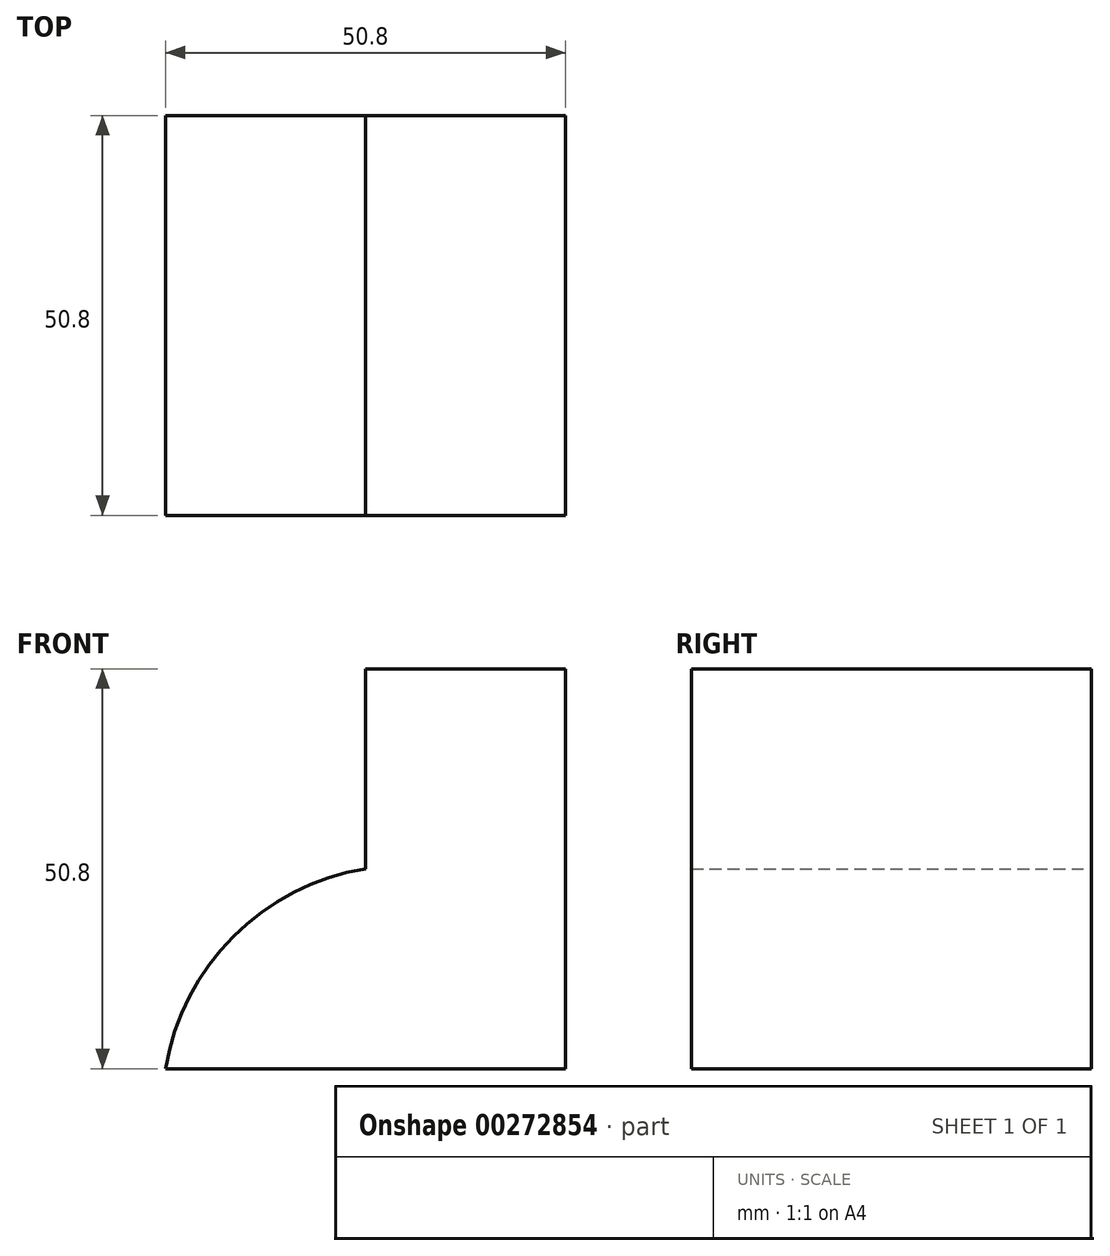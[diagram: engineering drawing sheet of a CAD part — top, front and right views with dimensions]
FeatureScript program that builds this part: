
annotation { "Feature Type Name" : "Feature", "Feature Type Description" : "" }
export const myFeature = defineFeature(function(context is Context, id is Id, definition is map)
    precondition{}
    {
        {
            var Q0;
            Q0=qCreatedBy(makeId("Front.planeOp"),FACE);
            var sketch = newSketch(context, id + "F0", { "sketchPlane" : qUnion([Q0])});
            skLineSegment(sketch, "E0", {"start": v(0, 0) * mm, "end": v(-50.8, 0) * mm});
            skLineSegment(sketch, "E1", {"start": v(0, 0) * mm, "end": v(0, 50.8) * mm});
            skLineSegment(sketch, "E2", {"start": v(0, 50.8) * mm, "end": v(-25.4, 50.8) * mm});
            skLineSegment(sketch, "E3", {"start": v(-25.4, 50.8) * mm, "end": v(-25.4, 25.4) * mm});
            skArc(sketch, "E4", {"start": v(-25.4, 25.4) * mm, "mid": v(-42.18, 16.78) * mm, "end": v(-50.8, 0) * mm});
            skSolve(sketch);
        }
        {
            var Q0;
            Q0 = qSketchRegion(id + "F0", true);
            extrude(context, id + "F1", {"entities" : qUnion([Q0]), "depth" : 50.8 * mm});
        }
    });
